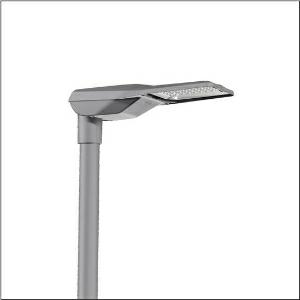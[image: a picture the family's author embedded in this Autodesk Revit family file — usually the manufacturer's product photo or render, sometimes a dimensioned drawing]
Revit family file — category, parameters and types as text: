
# Revit family: streetlight_sl_21_iq_mini___pl52_5xe2h31g08hb_1606
name_source: partatom
category: Lighting Fixtures
units: mm (PartAtom-declared; Revit-internal decimal feet)

## family parameters
Cut with Voids When Loaded = No
Host = Face
Light Source = No
Part Type = Normal
Room Calculation Point = No
Round Connector Dimension = Use Diameter
Shared = No

## types (1)
- --- (1 x LED, 9290 lm, 70.9 W, 3000K)
    Apparent Load = 71 VA
    CIE Flux Codes = 27 59 98 100 100
    Color Rendering = 70
    Color Temperature = 3000K
    Default Elevation = 1800 mm
    Description = Streetlight SL 21 iQ mini, mast luminaire, primary light control with lens, of PMMA, primary optical cover: cover, of toughened safety glass, transparent, light distribution: PL52, light emission: direct distribution, primary light characteristic: asymmetric, installation type: post-top, side-entry, LED, High Power LED, rated luminous flux: 9.290lm, luminous efficacy: 131lm/W, light colour: 730, colour temperature: 3000K, control gear: iQ Street-Remote, control: Street-Remote, Auto-Match, Temp-Guard, Lumen-Switch, Night-Set, Smart-Wire, Light-Fading, Desk-Remote (wireless, voltage-free reading and setting of iQ features in the workshop via application-optimized NFC function/RFID function), optimised constant luminous flux control (CLO 2.0), pre-setting: linear dimming characteristic, mains connection: 220..240V, AC, 50/60Hz, start of lifetime: 71W, end of service life: 75W, reduction: 31W, luminaire housing, of diecast aluminium, powder-coated, SITECO metallic grey (DB 702S), corrosivity category C5 high according to DIN EN ISO 12944, please order mast flange separately, inclination adjustable: 0°, 5°, 10°, 15°, sealing non-destructively replaceable, multi-level sealing system, length: 628mm, width: 235mm, height: 110mm, mast flange for spigot size: 42mm (side-entry): 5XC10008XM4, 60/48mm (side-entry/post-top): 5XC10108XM2, 76/60mm (side-entry/post-top): 5XC10108XM1, mounting height: 4..8m, protection rating (complete): IP66, insulation class (complete): insulation class II (safety insulation), certification: CE, ENEC, ENEC+, VDE, impact resistance: IK10, permissible operating ambient temperature for outdoor applications: -40..+50°C, standard-compliant lighting for roads and squares, packaging unit: 1 piece

Light Distribution: PL52
    Height = 110 mm
    Lamp = 1 x LED
    Lamp Light Flux = 9290 lm
    Lamp Power = 70.9 W
    Lamp count = 1
    Length = 625 mm
    Luminous efficacy = 131 lm/W
    Manufacturer = Siteco
    ModVariant = No
    Model = 5XE2H31G08HB
    Number of Poles = 1
    OnlyDefault = Yes
    Power Factor = 1
    Product Name = Streetlight SL 21 iQ mini | PL52
    Product group = mast luminaire | pylon top
    ProductGroupID = 6100
    Protection Class = Protection class II
    Protection Degree = IP 66
    RLX_Detail_Level = 1
    RLX_Emergency_Light_Flux = 0 lm
    RLX_Emergency_Type = 0
    RLX_Emergency_Type_DB = No
    RlxData = <blob elided: 35881 chars, md5=fd5d8b69>
    Socket = socket
    Standby Power = 0 W
    System Light Flux = 9290 lm
    System Power = 71 W
    Type Comments = factory setting: luminous flux: 100 % | dim-lin: 254 | 711 mA
    Type Image = l_1003519.jpg
    URL = http://relux.com
    VarID = @adj_157907
    Voltage = 0 V
    Weight = 0.00 kg
    Width = 234 mm

## geometry (parser evidence)
native form markers: Blend x4, Sweep x12
no freeform markers — native parametric forms only
